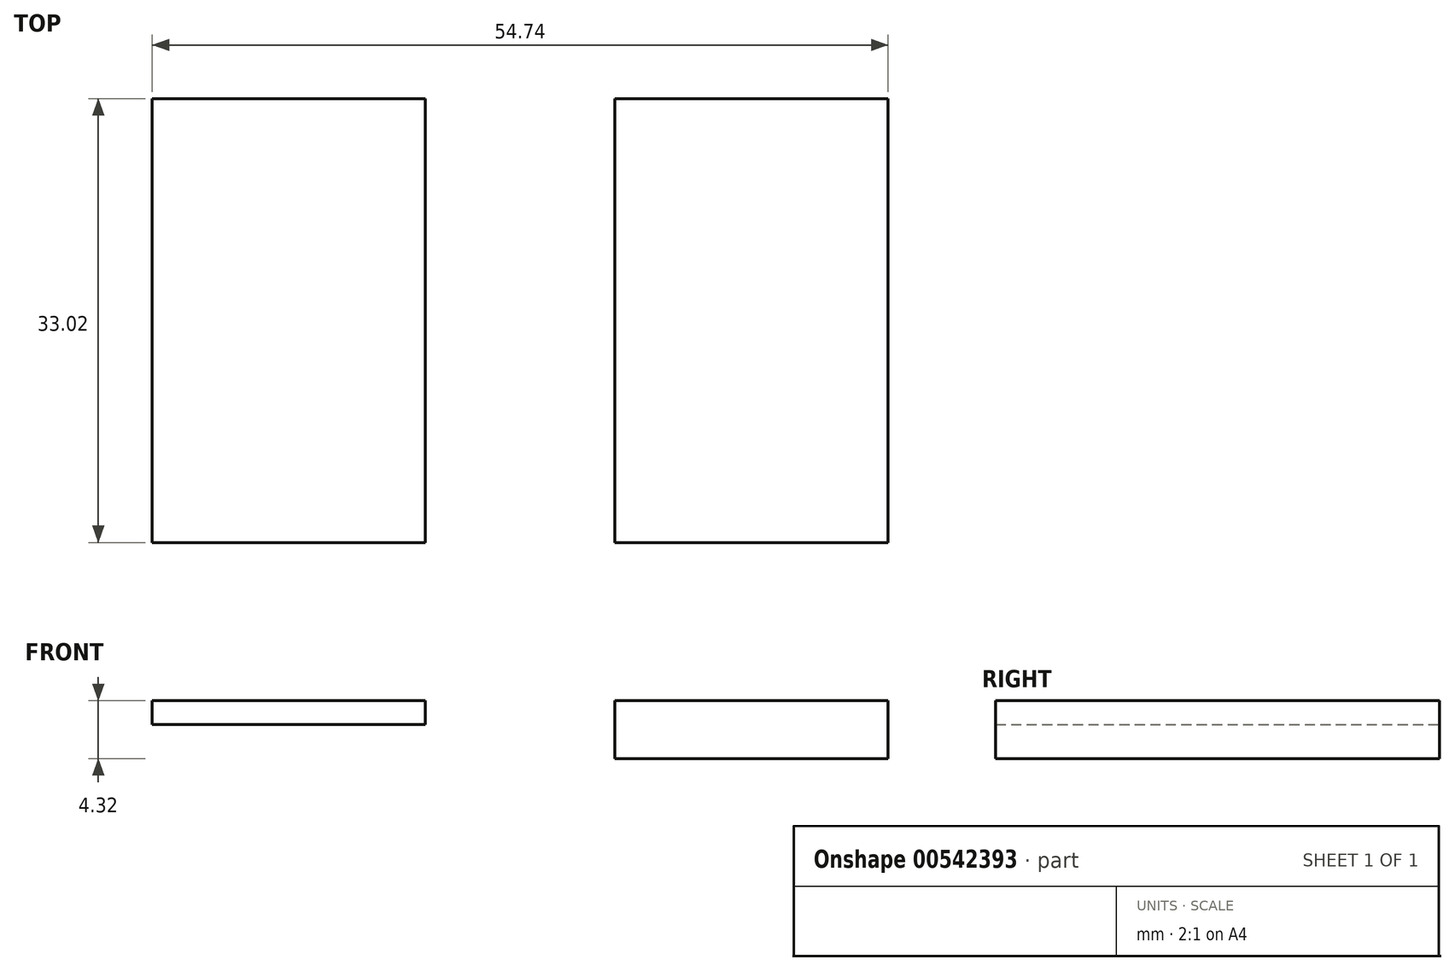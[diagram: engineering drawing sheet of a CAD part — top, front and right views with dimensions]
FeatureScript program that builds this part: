
annotation { "Feature Type Name" : "Feature", "Feature Type Description" : "" }
export const myFeature = defineFeature(function(context is Context, id is Id, definition is map)
    precondition{}
    {
        {
            var Q0;
            Q0=qCreatedBy(makeId("Front.planeOp"),FACE);
            var sketch = newSketch(context, id + "F0", { "sketchPlane" : qUnion([Q0])});
            skLineSegment(sketch, "E0.bottom", {"start": v(10.16, 0.89) * mm, "end": v(-10.16, 0.89) * mm});
            skLineSegment(sketch, "E0.top", {"start": v(10.16, -0.89) * mm, "end": v(-10.16, -0.89) * mm});
            skLineSegment(sketch, "E0.left", {"start": v(10.16, 0.89) * mm, "end": v(10.16, -0.89) * mm});
            skLineSegment(sketch, "E0.right", {"start": v(-10.16, 0.89) * mm, "end": v(-10.16, -0.89) * mm});
            skPoint(sketch, "E0.middle", {"position": v(0, 0) * mm});
            skLineSegment(sketch, "E1", {"start": v(24.26, 0.89) * mm, "end": v(24.26, -3.43) * mm});
            skLineSegment(sketch, "E2", {"start": v(24.26, -3.43) * mm, "end": v(44.58, -3.43) * mm});
            skLineSegment(sketch, "E3", {"start": v(44.58, -3.43) * mm, "end": v(44.58, 0.89) * mm});
            skLineSegment(sketch, "E4", {"start": v(44.58, 0.89) * mm, "end": v(24.26, 0.89) * mm});
            skSolve(sketch);
        }
        {
            var Q0;
            Q0=makeQuery(id+"F0.imprint","IMPRINT",FACE,{"disambiguationData":[TD([[makeQuery(id+"F0.imprint","IMPRINT",EDGE,{"derivedFrom":sQuery(id+"F0.wireOp",EDGE,"E0.bottom")}),1.0]])]});
            extrude(context, id + "F1", {"entities" : qUnion([Q0]), "depth" : 33.02 * mm, "offsetDistance" : 25.4 * mm});
        }
        {
            var Q0;
            Q0 = qSketchRegion(id + "F0", true);
            extrude(context, id + "F2", {"entities" : qUnion([Q0]), "operationType" : NewBodyOperationType.ADD, "depth" : 33.02 * mm, "offsetDistance" : 25.4 * mm});
        }
    });
